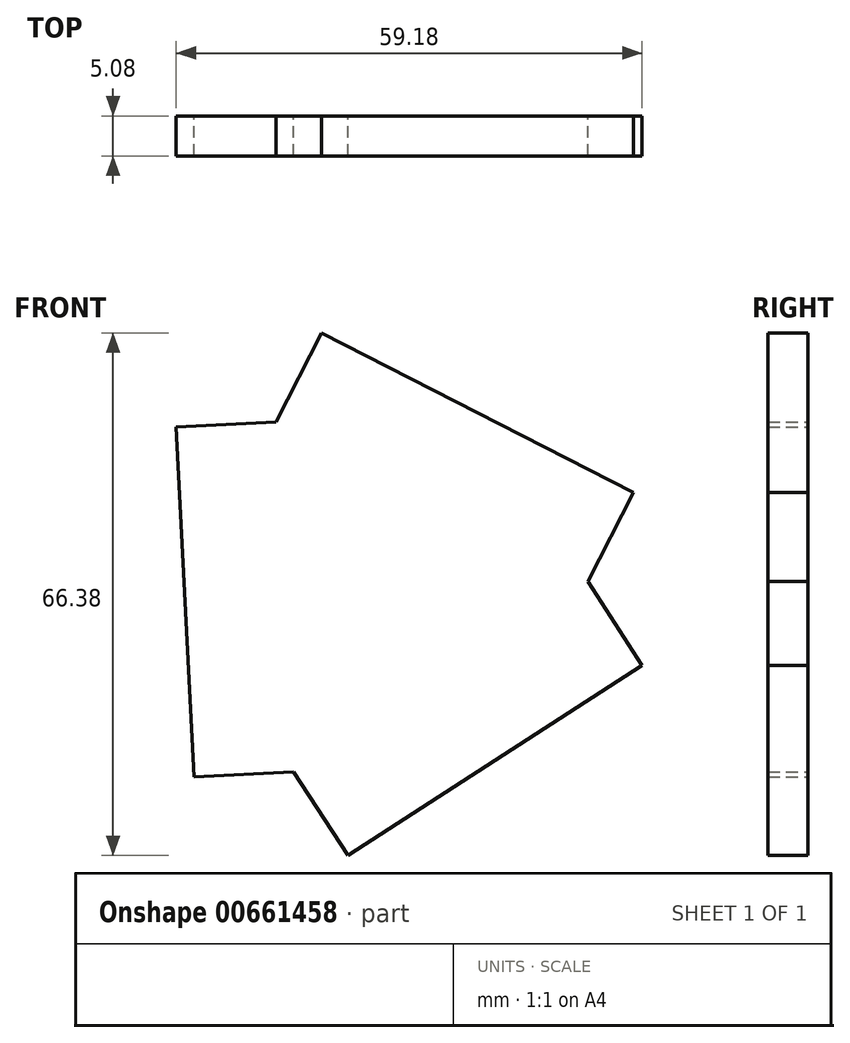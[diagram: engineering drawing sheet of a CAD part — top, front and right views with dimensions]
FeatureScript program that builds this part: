
annotation { "Feature Type Name" : "Feature", "Feature Type Description" : "" }
export const myFeature = defineFeature(function(context is Context, id is Id, definition is map)
    precondition{}
    {
        {
            var Q0;
            Q0=qCreatedBy(makeId("Front.planeOp"),FACE);
            var sketch = newSketch(context, id + "F0", { "sketchPlane" : qUnion([Q0])});
            skFitSpline(sketch, "E0", {"points": [v(18.51, 3.03) * mm, v(10.13, 6.53) * mm, v(11.5, -7.42) * mm, v(11.58, -5.68) * mm, v(12.75, -1.4) * mm, v(18.83, -0.34) * mm, v(22.4, 3.27) * mm, v(17.08, 9.55) * mm, v(8.62, 9.56) * mm, v(12.22, 9.36) * mm, v(18.9, 6.31) * mm, v(20.4, 3.15) * mm, v(18.51, 3.03) * mm]});
            skSolve(sketch);
        }
        {
            var Q0;
            Q0=qCreatedBy(makeId("Front.planeOp"),FACE);
            var sketch = newSketch(context, id + "F1", { "sketchPlane" : qUnion([Q0])});
            skCircle(sketch, "E1.cCircle", {"center": v(13.93, 0) * mm, "radius": 12.84 * mm, "construction": true});
            skLineSegment(sketch, "E1.0", {"start": v(-0.02, 21.56) * mm, "end": v(39.58, 1.3) * mm});
            skLineSegment(sketch, "E1.1", {"start": v(39.58, 1.3) * mm, "end": v(2.24, -22.86) * mm});
            skLineSegment(sketch, "E1.2", {"start": v(2.24, -22.86) * mm, "end": v(-0.02, 21.56) * mm});
            skPoint(sketch, "E1.0.midPoint", {"position": v(19.78, 11.43) * mm});
            skSolve(sketch);
        }
        {
            var Q0;
            Q0=makeQuery(id+"F1.imprint","IMPRINT",FACE,{"disambiguationData":[TD([[makeQuery(id+"F1.imprint","IMPRINT",EDGE,{"derivedFrom":sQuery(id+"F1.wireOp",EDGE,"E1.0")}),-1.0]])]});
            extrude(context, id + "F2", {"entities" : qUnion([Q0]), "depth" : 5.08 * mm, "offsetDistance" : 25.4 * mm});
        }
        {
            var Q0;
            Q0=makeQuery(id+"F2.opExtrude","SWEPT_FACE",FACE,{"disambiguationData":[OSD([sQuery(id+"F1.wireOp",EDGE,"E1.2")])]});
            extrude(context, id + "F3", {"entities" : qUnion([Q0]), "operationType" : NewBodyOperationType.ADD, "depth" : 12.7 * mm, "offsetDistance" : 25.4 * mm});
        }
        {
            var Q0;
            Q0=makeQuery(id+"F2.opExtrude","SWEPT_FACE",FACE,{"disambiguationData":[OSD([sQuery(id+"F1.wireOp",EDGE,"E1.1")])]});
            extrude(context, id + "F4", {"entities" : qUnion([Q0]), "operationType" : NewBodyOperationType.ADD, "depth" : 12.7 * mm, "offsetDistance" : 25.4 * mm});
        }
        {
            var Q0;
            Q0=makeQuery(id+"F2.opExtrude","SWEPT_FACE",FACE,{"disambiguationData":[OSD([sQuery(id+"F1.wireOp",EDGE,"E1.0")])]});
            extrude(context, id + "F5", {"entities" : qUnion([Q0]), "operationType" : NewBodyOperationType.ADD, "depth" : 12.7 * mm, "offsetDistance" : 25.4 * mm});
        }
        {
            var Q0;
            Q0=sQuery(id+"F0.wireOp",EDGE,"E0");
            extrude(context, id + "F6", {"bodyType" : ToolBodyType.SURFACE, "surfaceEntities" : qUnion([Q0]), "depth" : 7.62 * mm, "offsetDistance" : 25.4 * mm});
        }
    });
